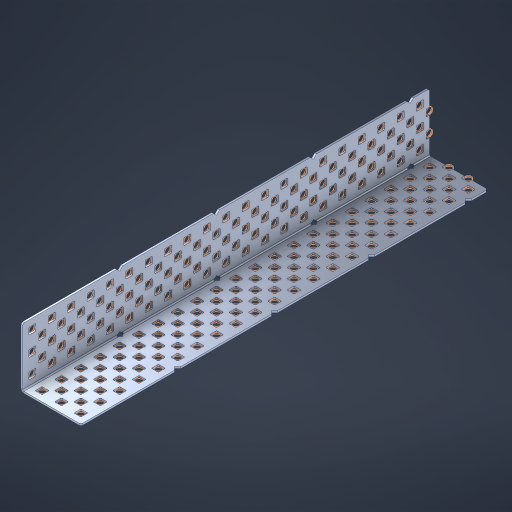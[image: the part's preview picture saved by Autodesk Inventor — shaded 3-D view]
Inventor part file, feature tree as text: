
AUTODESK INVENTOR PART (.ipt)
format: ipt  version: 2023 (Build 270158000, 158)  size: 2,264,064 bytes
history: native  units: in
note: dims shown in document units (in); Inventor stores cm internally (conversion verified against a paired STEP export)
features: other x216, extrude x208, sheet_metal_op x8, sketch x7, pattern_linear x3, mirror x1, chamfer x1
ambient origin geometry x8: Origin, YZ Plane, XZ Plane, XY Plane, X Axis, Y Axis, Z Axis, Center Point
bodies: Solid1 (feature_tree), Body (feature_tree)
feature tree (444):
  sheet_metal_op  "Flanges"
  sheet_metal_op  "Body Pattern"
  pattern_linear  "Center Double"  Spacing1=1.5in  [1 undecoded]
  pattern_linear  "Center Pattern"  Spacing1=0.1875in  [1 undecoded]
  other  "Arc Length"
  pattern_linear  "Notch Pattern"  Spacing1=0.0469in  [1 undecoded]
  other  "Diagonal Plane"
  mirror  "Everything Mirrored"
  chamfer  "End Chamfer"
  sketch  "Sketch1"  dims[d0=1.5in]
  other  "Plate1"
  sketch  "Sketch2"  dims[d1=10.5in]
  other  "Plate2"
  sheet_metal_op  "Bend1"
  sheet_metal_op  "Corner1"
  sketch  "Sketch8"  dims[d2=0.0469in]
  sketch  "Sketch9"  dims[d3=0.0469in]
  other  "Srf91"
  sheet_metal_op  "Body Pattern Sketch"
  other  "Srf92"
  sketch  "Sketch13"  dims[d4=0.0234in]
  sketch  "Sketch15"  dims[d5=0.0938in]
  sketch  "Sketch16"  dims[d6=0.0469in d7=1.5in d8=90.0deg d9=0.0312in d10=0.1875in d11=0.0469in d12=0.0469in d49=0.182in d50=0.02in d52=0.25in d53=0.0469in d54=0.0in d55=0.172in d56=1.0in d57=0.0in d85=0.1473in d86=0.1659in d89=0.0469in d90=0.0in d91=0.04in d92=0.0491in d95=2.5in d96=0.04in d97=0.25in d98=45.0deg d106=0.182in d107=0.02in d110=0.0469in d111=0.0in d112=0.172in d113=0.5in d114=0.0in d117=0.5in d126=0.0491in d127=0.1227in d128=0.08in d129=0.04in d130=2.5in d131=0.25in d132=8.2677in d134=0.5in d135=1.1811in d137=0.5in d140=0.5in d141=1.0in d142=0.3937in d144=0.5in d145=0.071in d146=0.7874in d148=0.5in]
  other  "Srf786"
  other  "Srf856"
  other  "Srf889"
  other  "Srf890"
  other  "Srf891"
  other  "Srf1275"
  other  "Srf1276"
  other  "Srf1278"
  other  "Srf1277"
  other  "Srf1285"
  other  "Srf1286"
  other  "Srf1287"
  other  "Srf1445"
  other  "Srf1446"
  other  "Srf1447"
  other  "Srf1448"
  other  "Srf1449"
  other  "Srf1537"
  other  "Srf1538"
  other  "Srf1539"
  other  "Srf1540"
  other  "Srf1541"
  other  "Srf1807"
  other  "Srf1808"
  other  "Srf1809"
  other  "Srf1810"
  other  "Srf1811"
  other  "Srf1812"
  other  "Srf1813"
  other  "Srf1814"
  other  "Srf1815"
  other  "Srf1816"
  other  "Srf1817"
  other  "Srf1818"
  other  "Srf1959"
  other  "Srf1960"
  other  "Srf1961"
  other  "Srf1962"
  other  "Srf1963"
  other  "Srf1964"
  other  "Srf1965"
  other  "Srf1966"
  other  "Srf1967"
  other  "Srf1968"
  other  "Srf1969"
  other  "Srf1970"
  other  "Srf2009"
  other  "Srf2010"
  other  "Srf2011"
  other  "Srf2012"
  other  "Srf2013"
  other  "Srf2014"
  other  "Srf2015"
  other  "Srf2016"
  other  "Srf2017"
  other  "Srf2018"
  other  "Srf2019"
  other  "Srf2020"
  other  "Srf2021"
  other  "Srf2022"
  other  "Srf2023"
  other  "Srf2024"
  other  "Srf2025"
  other  "Srf2026"
  other  "Srf2027"
  other  "Srf2028"
  other  "Srf2029"
  other  "Srf2043"
  other  "Srf2044"
  other  "Srf2045"
  other  "Srf2046"
  other  "Srf2047"
  other  "Srf2048"
  other  "Srf2049"
  other  "Srf2050"
  other  "Srf2051"
  other  "Srf2052"
  other  "Srf2053"
  other  "Srf2054"
  other  "Srf2055"
  other  "Srf2056"
  other  "Srf2057"
  other  "Srf2058"
  other  "Srf2059"
  other  "Srf2060"
  other  "Srf2061"
  other  "Srf2062"
  other  "Srf2076"
  other  "Srf2077"
  other  "Srf2078"
  other  "Srf2079"
  other  "Srf2080"
  other  "Srf2081"
  other  "Srf2082"
  other  "Srf2083"
  other  "Srf2084"
  other  "Srf2085"
  other  "Srf2086"
  other  "Srf2087"
  other  "Srf2088"
  other  "Srf2089"
  other  "Srf2090"
  other  "Srf2091"
  other  "Srf2092"
  other  "Srf2093"
  other  "Srf2094"
  other  "Srf2095"
  other  "Srf2096"
  other  "Srf2097"
  other  "Srf2098"
  other  "Srf2099"
  other  "Srf2100"
  other  "Srf2101"
  other  "Srf2102"
  other  "Srf2103"
  other  "Srf2104"
  other  "Srf2105"
  other  "Srf2106"
  other  "Srf2107"
  other  "Srf2108"
  other  "Srf2109"
  other  "Srf2110"
  other  "Srf2111"
  other  "Srf2112"
  other  "Srf2113"
  other  "Srf2114"
  other  "Srf2115"
  other  "Srf2116"
  other  "Srf2117"
  other  "Srf2118"
  other  "Srf2119"
  other  "Srf2120"
  other  "Srf2121"
  other  "Srf2122"
  other  "Srf2123"
  other  "Srf2124"
  other  "Srf2125"
  other  "Srf2126"
  other  "Srf2127"
  other  "Srf2128"
  other  "Srf2129"
  other  "Srf2130"
  other  "Srf2131"
  other  "Srf2132"
  other  "Srf2133"
  other  "Srf2134"
  other  "Srf2135"
  other  "Srf2136"
  other  "Srf2179"
  other  "Srf2180"
  other  "Srf2181"
  other  "Srf2182"
  other  "Srf2183"
  other  "Srf2184"
  other  "Srf2185"
  other  "Srf2186"
  other  "Srf2187"
  other  "Srf2188"
  other  "Srf2189"
  other  "Srf2190"
  other  "Srf2191"
  other  "Srf2192"
  other  "Srf2193"
  other  "Srf2194"
  other  "Srf2195"
  other  "Srf2196"
  other  "Srf2197"
  other  "Srf2198"
  other  "Srf2199"
  other  "Srf2200"
  other  "Srf2201"
  other  "Srf2202"
  other  "Srf2203"
  other  "Srf2204"
  other  "Srf2205"
  other  "Srf2206"
  other  "Srf2207"
  other  "Srf2208"
  other  "Srf2209"
  other  "Srf2210"
  other  "Srf2211"
  other  "Srf2212"
  other  "Srf2213"
  other  "Srf2214"
  other  "Srf2215"
  other  "Srf2216"
  other  "Srf2217"
  other  "Srf2218"
  other  "Srf2219"
  other  "Srf2220"
  other  "Srf2221"
  other  "Srf2222"
  other  "Srf2223"
  other  "Srf2224"
  other  "Srf2225"
  other  "Srf2226"
  other  "Srf2227"
  other  "Srf2228"
  other  "Srf2229"
  other  "Srf2230"
  other  "Srf2231"
  other  "Srf2232"
  other  "Srf2233"
  other  "Srf2234"
  other  "Srf2235"
  other  "Srf2236"
  other  "Srf2237"
  other  "Srf2238"
  sheet_metal_op  "Body Stamp"
  sheet_metal_op  "Body Circle"
  other  "Center Stamp"
  other  "Center Circle"
  sheet_metal_op  "Notch"
  extrude  "ExtrusionSrf92"  Depth=0.0469in
  extrude  "ExtrusionSrf856"  Depth=0.182in
  extrude  "ExtrusionSrf889"  Depth=0.02in
  extrude  "ExtrusionSrf890"  Depth=0.25in
  extrude  "ExtrusionSrf891"  Depth=0.0469in
  extrude  "ExtrusionSrf1275"  TaperAngle=0.0deg  [1 undecoded]
  extrude  "ExtrusionSrf1276"  Depth=0.5in
  extrude  "ExtrusionSrf1277"  Depth=1.0in TaperAngle=0.0deg
  extrude  "ExtrusionSrf1345"  Depth=0.5in
  extrude  "ExtrusionSrf1346"  Depth=0.5in
  extrude  "ExtrusionSrf1347"  Depth=0.0469in
  extrude  "ExtrusionSrf1348"  Depth=0.5in TaperAngle=0.0deg
  extrude  "ExtrusionSrf1445"  Depth=0.5in
  extrude  "ExtrusionSrf1446"  Depth=0.25in TaperAngle=45.0deg
  extrude  "ExtrusionSrf1447"  Depth=0.182in
  extrude  "ExtrusionSrf1448"  Depth=0.02in
  extrude  "ExtrusionSrf1449"  Depth=0.0469in
  extrude  "ExtrusionSrf1537"  TaperAngle=0.0deg  [1 undecoded]
  extrude  "ExtrusionSrf1538"  Depth=0.5in
  extrude  "ExtrusionSrf1539"  Depth=0.5in TaperAngle=0.0deg
  extrude  "ExtrusionSrf1540"  Depth=0.5in
  extrude  "ExtrusionSrf1541"  Depth=0.5in
  extrude  "ExtrusionSrf1807"  Depth=0.5in
  extrude  "ExtrusionSrf1808"  Depth=0.5in
  extrude  "ExtrusionSrf1809"  Depth=0.5in
  extrude  "ExtrusionSrf1810"  Depth=0.5in
  extrude  "ExtrusionSrf1811"  Depth=0.25in
  extrude  "ExtrusionSrf1812"  Depth=0.5in
  extrude  "ExtrusionSrf1813"  Depth=0.5in
  extrude  "ExtrusionSrf1814"  Depth=0.5in
  extrude  "ExtrusionSrf1815"  Depth=1.0in
  extrude  "ExtrusionSrf1816"  Depth=0.3937in
  extrude  "ExtrusionSrf1817"  Depth=0.5in
  extrude  "ExtrusionSrf1818"  Depth=0.5in
  extrude  "ExtrusionSrf1959"  [1 undecoded]
  extrude  "ExtrusionSrf1960"  [1 undecoded]
  extrude  "ExtrusionSrf1961"  [1 undecoded]
  extrude  "ExtrusionSrf1962"  [1 undecoded]
  extrude  "ExtrusionSrf1963"  [1 undecoded]
  extrude  "ExtrusionSrf1964"  [1 undecoded]
  extrude  "ExtrusionSrf1965"  [1 undecoded]
  extrude  "ExtrusionSrf1966"  [1 undecoded]
  extrude  "ExtrusionSrf1967"  [1 undecoded]
  extrude  "ExtrusionSrf1968"  [1 undecoded]
  extrude  "ExtrusionSrf1969"  [1 undecoded]
  extrude  "ExtrusionSrf1970"  [1 undecoded]
  extrude  "ExtrusionSrf2009"  [1 undecoded]
  extrude  "ExtrusionSrf2010"  [1 undecoded]
  extrude  "ExtrusionSrf2011"  [1 undecoded]
  extrude  "ExtrusionSrf2012"  [1 undecoded]
  extrude  "ExtrusionSrf2013"  [1 undecoded]
  extrude  "ExtrusionSrf2014"  [1 undecoded]
  extrude  "ExtrusionSrf2015"  [1 undecoded]
  extrude  "ExtrusionSrf2016"  [1 undecoded]
  extrude  "ExtrusionSrf2017"  [1 undecoded]
  extrude  "ExtrusionSrf2018"  [1 undecoded]
  extrude  "ExtrusionSrf2019"  [1 undecoded]
  extrude  "ExtrusionSrf2020"  [1 undecoded]
  extrude  "ExtrusionSrf2021"  [1 undecoded]
  extrude  "ExtrusionSrf2022"  [1 undecoded]
  extrude  "ExtrusionSrf2023"  [1 undecoded]
  extrude  "ExtrusionSrf2024"  [1 undecoded]
  extrude  "ExtrusionSrf2025"  [1 undecoded]
  extrude  "ExtrusionSrf2026"  [1 undecoded]
  extrude  "ExtrusionSrf2027"  [1 undecoded]
  extrude  "ExtrusionSrf2028"  [1 undecoded]
  extrude  "ExtrusionSrf2029"  [1 undecoded]
  extrude  "ExtrusionSrf2043"  [1 undecoded]
  extrude  "ExtrusionSrf2044"  [1 undecoded]
  extrude  "ExtrusionSrf2045"  [1 undecoded]
  extrude  "ExtrusionSrf2046"  [1 undecoded]
  extrude  "ExtrusionSrf2047"  [1 undecoded]
  extrude  "ExtrusionSrf2048"  [1 undecoded]
  extrude  "ExtrusionSrf2049"  [1 undecoded]
  extrude  "ExtrusionSrf2050"  [1 undecoded]
  extrude  "ExtrusionSrf2051"  [1 undecoded]
  extrude  "ExtrusionSrf2052"  [1 undecoded]
  extrude  "ExtrusionSrf2053"  [1 undecoded]
  extrude  "ExtrusionSrf2054"  [1 undecoded]
  extrude  "ExtrusionSrf2055"  [1 undecoded]
  extrude  "ExtrusionSrf2056"  [1 undecoded]
  extrude  "ExtrusionSrf2057"  [1 undecoded]
  extrude  "ExtrusionSrf2058"  [1 undecoded]
  extrude  "ExtrusionSrf2059"  [1 undecoded]
  extrude  "ExtrusionSrf2060"  [1 undecoded]
  extrude  "ExtrusionSrf2061"  [1 undecoded]
  extrude  "ExtrusionSrf2062"  [1 undecoded]
  extrude  "ExtrusionSrf2076"  [1 undecoded]
  extrude  "ExtrusionSrf2077"  [1 undecoded]
  extrude  "ExtrusionSrf2078"  [1 undecoded]
  extrude  "ExtrusionSrf2079"  [1 undecoded]
  extrude  "ExtrusionSrf2080"  [1 undecoded]
  extrude  "ExtrusionSrf2081"  [1 undecoded]
  extrude  "ExtrusionSrf2082"  [1 undecoded]
  extrude  "ExtrusionSrf2083"  [1 undecoded]
  extrude  "ExtrusionSrf2084"  [1 undecoded]
  extrude  "ExtrusionSrf2085"  [1 undecoded]
  extrude  "ExtrusionSrf2086"  [1 undecoded]
  extrude  "ExtrusionSrf2087"  [1 undecoded]
  extrude  "ExtrusionSrf2088"  [1 undecoded]
  extrude  "ExtrusionSrf2089"  [1 undecoded]
  extrude  "ExtrusionSrf2090"  [1 undecoded]
  extrude  "ExtrusionSrf2091"  [1 undecoded]
  extrude  "ExtrusionSrf2092"  [1 undecoded]
  extrude  "ExtrusionSrf2093"  [1 undecoded]
  extrude  "ExtrusionSrf2094"  [1 undecoded]
  extrude  "ExtrusionSrf2095"  [1 undecoded]
  extrude  "ExtrusionSrf2096"  [1 undecoded]
  extrude  "ExtrusionSrf2097"  [1 undecoded]
  extrude  "ExtrusionSrf2098"  [1 undecoded]
  extrude  "ExtrusionSrf2099"  [1 undecoded]
  extrude  "ExtrusionSrf2100"  [1 undecoded]
  extrude  "ExtrusionSrf2101"  [1 undecoded]
  extrude  "ExtrusionSrf2102"  [1 undecoded]
  extrude  "ExtrusionSrf2103"  [1 undecoded]
  extrude  "ExtrusionSrf2104"  [1 undecoded]
  extrude  "ExtrusionSrf2105"  [1 undecoded]
  extrude  "ExtrusionSrf2106"  [1 undecoded]
  extrude  "ExtrusionSrf2107"  [1 undecoded]
  extrude  "ExtrusionSrf2108"  [1 undecoded]
  extrude  "ExtrusionSrf2109"  [1 undecoded]
  extrude  "ExtrusionSrf2110"  [1 undecoded]
  extrude  "ExtrusionSrf2111"  [1 undecoded]
  extrude  "ExtrusionSrf2112"  [1 undecoded]
  extrude  "ExtrusionSrf2113"  [1 undecoded]
  extrude  "ExtrusionSrf2114"  [1 undecoded]
  extrude  "ExtrusionSrf2115"  [1 undecoded]
  extrude  "ExtrusionSrf2116"  [1 undecoded]
  extrude  "ExtrusionSrf2117"  [1 undecoded]
  extrude  "ExtrusionSrf2118"  [1 undecoded]
  extrude  "ExtrusionSrf2119"  [1 undecoded]
  extrude  "ExtrusionSrf2120"  [1 undecoded]
  extrude  "ExtrusionSrf2121"  [1 undecoded]
  extrude  "ExtrusionSrf2122"  [1 undecoded]
  extrude  "ExtrusionSrf2123"  [1 undecoded]
  extrude  "ExtrusionSrf2124"  [1 undecoded]
  extrude  "ExtrusionSrf2125"  [1 undecoded]
  extrude  "ExtrusionSrf2126"  [1 undecoded]
  extrude  "ExtrusionSrf2127"  [1 undecoded]
  extrude  "ExtrusionSrf2128"  [1 undecoded]
  extrude  "ExtrusionSrf2129"  [1 undecoded]
  extrude  "ExtrusionSrf2130"  [1 undecoded]
  extrude  "ExtrusionSrf2131"  [1 undecoded]
  extrude  "ExtrusionSrf2132"  [1 undecoded]
  extrude  "ExtrusionSrf2133"  [1 undecoded]
  extrude  "ExtrusionSrf2134"  [1 undecoded]
  extrude  "ExtrusionSrf2135"  [1 undecoded]
  extrude  "ExtrusionSrf2136"  [1 undecoded]
  extrude  "ExtrusionSrf2179"  [1 undecoded]
  extrude  "ExtrusionSrf2180"  [1 undecoded]
  extrude  "ExtrusionSrf2181"  [1 undecoded]
  extrude  "ExtrusionSrf2182"  [1 undecoded]
  extrude  "ExtrusionSrf2183"  [1 undecoded]
  extrude  "ExtrusionSrf2184"  [1 undecoded]
  extrude  "ExtrusionSrf2185"  [1 undecoded]
  extrude  "ExtrusionSrf2186"  [1 undecoded]
  extrude  "ExtrusionSrf2187"  [1 undecoded]
  extrude  "ExtrusionSrf2188"  [1 undecoded]
  extrude  "ExtrusionSrf2189"  [1 undecoded]
  extrude  "ExtrusionSrf2190"  [1 undecoded]
  extrude  "ExtrusionSrf2191"  [1 undecoded]
  extrude  "ExtrusionSrf2192"  [1 undecoded]
  extrude  "ExtrusionSrf2193"  [1 undecoded]
  extrude  "ExtrusionSrf2194"  [1 undecoded]
  extrude  "ExtrusionSrf2195"  [1 undecoded]
  extrude  "ExtrusionSrf2196"  [1 undecoded]
  extrude  "ExtrusionSrf2197"  [1 undecoded]
  extrude  "ExtrusionSrf2198"  [1 undecoded]
  extrude  "ExtrusionSrf2199"  [1 undecoded]
  extrude  "ExtrusionSrf2200"  [1 undecoded]
  extrude  "ExtrusionSrf2201"  [1 undecoded]
  extrude  "ExtrusionSrf2202"  [1 undecoded]
  extrude  "ExtrusionSrf2203"  [1 undecoded]
  extrude  "ExtrusionSrf2204"  [1 undecoded]
  extrude  "ExtrusionSrf2205"  [1 undecoded]
  extrude  "ExtrusionSrf2206"  [1 undecoded]
  extrude  "ExtrusionSrf2207"  [1 undecoded]
  extrude  "ExtrusionSrf2208"  [1 undecoded]
  extrude  "ExtrusionSrf2209"  [1 undecoded]
  extrude  "ExtrusionSrf2210"  [1 undecoded]
  extrude  "ExtrusionSrf2211"  [1 undecoded]
  extrude  "ExtrusionSrf2212"  [1 undecoded]
  extrude  "ExtrusionSrf2213"  [1 undecoded]
  extrude  "ExtrusionSrf2214"  [1 undecoded]
  extrude  "ExtrusionSrf2215"  [1 undecoded]
  extrude  "ExtrusionSrf2216"  [1 undecoded]
  extrude  "ExtrusionSrf2217"  [1 undecoded]
  extrude  "ExtrusionSrf2218"  [1 undecoded]
  extrude  "ExtrusionSrf2219"  [1 undecoded]
  extrude  "ExtrusionSrf2220"  [1 undecoded]
  extrude  "ExtrusionSrf2221"  [1 undecoded]
  extrude  "ExtrusionSrf2222"  [1 undecoded]
  extrude  "ExtrusionSrf2223"  [1 undecoded]
  extrude  "ExtrusionSrf2224"  [1 undecoded]
  extrude  "ExtrusionSrf2225"  [1 undecoded]
  extrude  "ExtrusionSrf2226"  [1 undecoded]
  extrude  "ExtrusionSrf2227"  [1 undecoded]
  extrude  "ExtrusionSrf2228"  [1 undecoded]
  extrude  "ExtrusionSrf2229"  [1 undecoded]
  extrude  "ExtrusionSrf2230"  [1 undecoded]
  extrude  "ExtrusionSrf2231"  [1 undecoded]
  extrude  "ExtrusionSrf2232"  [1 undecoded]
  extrude  "ExtrusionSrf2233"  [1 undecoded]
  extrude  "ExtrusionSrf2234"  [1 undecoded]
  extrude  "ExtrusionSrf2235"  [1 undecoded]
  extrude  "ExtrusionSrf2236"  [1 undecoded]
  extrude  "ExtrusionSrf2237"  [1 undecoded]
  extrude  "ExtrusionSrf2238"  [1 undecoded]
note: 179 required parameter values undecoded (feature->parameter linkage not recoverable at this tier; creation-order binding heuristic only, values carry confidence <= 0.55)
